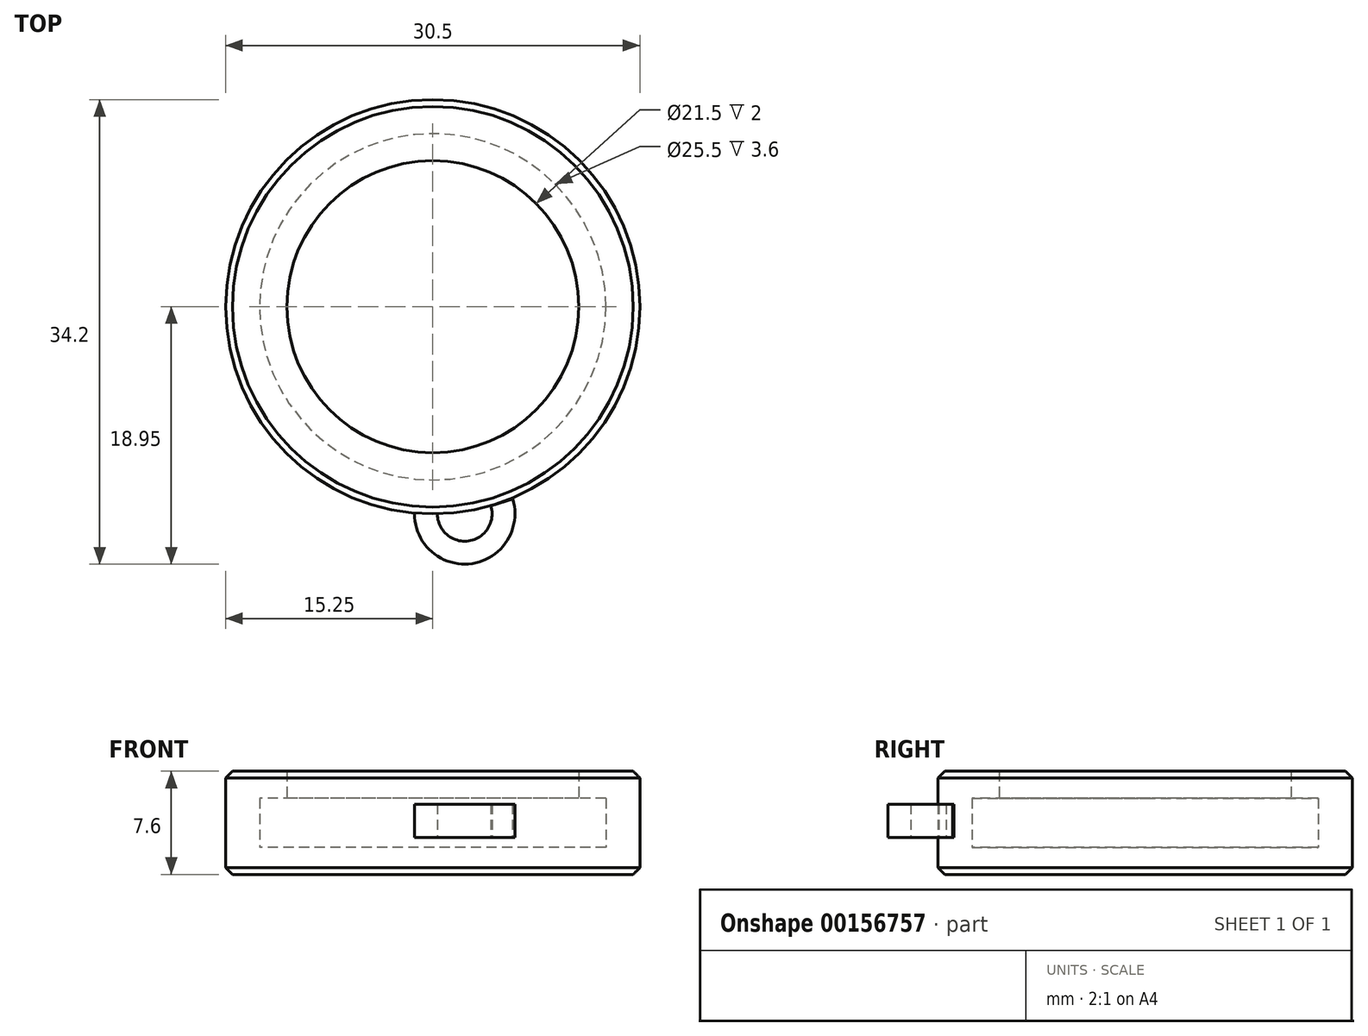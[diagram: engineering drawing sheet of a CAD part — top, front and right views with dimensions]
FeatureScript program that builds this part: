
annotation { "Feature Type Name" : "Feature", "Feature Type Description" : "" }
export const myFeature = defineFeature(function(context is Context, id is Id, definition is map)
    precondition{}
    {
        {
            var Q0;
            Q0=qCreatedBy(makeId("Top.planeOp"),FACE);
            var sketch = newSketch(context, id + "F0", { "sketchPlane" : qUnion([Q0])});
            skCircle(sketch, "E0", {"center": v(0, 0) * mm, "radius": 12.75 * mm});
            skCircle(sketch, "E1.0", {"center": v(0, 0) * mm, "radius": 15.25 * mm});
            skSolve(sketch);
        }
        {
            var Q0;
            Q0=makeQuery(id+"F0.imprint","IMPRINT",FACE,{"disambiguationData":[TD([[makeQuery(id+"F0.imprint","IMPRINT",EDGE,{"derivedFrom":sQuery(id+"F0.wireOp",EDGE,"E0")}),-1.0]])]});
            extrude(context, id + "F1", {"entities" : qUnion([Q0]), "depth" : 3.6 * mm});
        }
        {
            var Q0;
            Q0=makeQuery(id+"F0.imprint","IMPRINT",FACE,{"disambiguationData":[TD([[makeQuery(id+"F0.imprint","IMPRINT",EDGE,{"derivedFrom":sQuery(id+"F0.wireOp",EDGE,"E0")}),1.0]])]});
            var Q1;
            Q1=makeQuery(id+"F0.imprint","IMPRINT",FACE,{"disambiguationData":[TD([[makeQuery(id+"F0.imprint","IMPRINT",EDGE,{"derivedFrom":sQuery(id+"F0.wireOp",EDGE,"E0")}),-1.0]])]});
            extrude(context, id + "F2", {"entities" : qUnion([Q0, Q1]), "operationType" : NewBodyOperationType.ADD, "oppositeDirection" : true, "depth" : 2 * mm});
        }
        {
            var Q0;
            Q0=makeQuery(id+"F2.opExtrude","CAP_EDGE",EDGE,{"disambiguationData":[OSD([sQuery(id+"F0.wireOp",EDGE,"E1.0")])],"isStart":false});
            chamfer(context, id + "F3", {"entities" : qUnion([Q0]), "width" : 0.5 * mm, "tangentPropagation" : true});
        }
        {
            var Q0;
            Q0=makeQuery(id+"F1.opExtrude","CAP_FACE",FACE,{"disambiguationData":[OSD([sQuery(id+"F0.wireOp",EDGE,"E0"),sQuery(id+"F0.wireOp",EDGE,"E1.0")])],"isStart":false});
            var sketch = newSketch(context, id + "F4", { "sketchPlane" : qUnion([Q0])});
            skCircle(sketch, "E2.0", {"center": v(0, 0) * mm, "radius": 10.75 * mm});
            skSolve(sketch);
        }
        {
            var Q0;
            Q0=makeQuery(id+"F4.imprint","IMPRINT",FACE,{"disambiguationData":[TD([[makeQuery(id+"F4.imprint","IMPRINT",EDGE,{"derivedFrom":sQuery(id+"F4.wireOp",EDGE,"E2.0")}),-1.0]])]});
            var Q1;
            Q1=makeQuery(id+"F4.imprint","IMPRINT",FACE,{"disambiguationData":[TD([[makeQuery(id+"F4.imprint","IMPRINT",EDGE,{"derivedFrom":makeQuery(id+"F1.opExtrude","CAP_EDGE",EDGE,{"disambiguationData":[OSD([sQuery(id+"F0.wireOp",EDGE,"E0")])],"isStart":false})}),-1.0]])]});
            extrude(context, id + "F5", {"entities" : qUnion([Q0, Q1]), "operationType" : NewBodyOperationType.ADD, "depth" : 2 * mm});
        }
        {
            var Q0;
            Q0=makeQuery(id+"F5.opExtrude","CAP_EDGE",EDGE,{"disambiguationData":[OSD([sQuery(id+"F0.wireOp",EDGE,"E1.0")])],"isStart":false});
            chamfer(context, id + "F6", {"entities" : qUnion([Q0]), "width" : 0.5 * mm, "tangentPropagation" : true});
        }
        {
            var Q0;
            Q0=qCreatedBy(makeId("Front.planeOp"),FACE);
            cPlane(context, id + "F7", {"entities" : qUnion([Q0]), "cplaneType" : CPlaneType.OFFSET, "offset" : 15.25 * mm, "width" : 150 * mm, "height" : 150 * mm});
        }
        {
            var Q0;
            Q0=qCreatedBy(id+"F7.planeOp",FACE);
            var sketch = newSketch(context, id + "F8", { "sketchPlane" : qUnion([Q0])});
            skLineSegment(sketch, "E3.bottom", {"start": v(-1.35, 3.17) * mm, "end": v(0.33, 3.17) * mm});
            skLineSegment(sketch, "E3.top", {"start": v(-1.35, 0.7) * mm, "end": v(0.33, 0.7) * mm});
            skLineSegment(sketch, "E3.left", {"start": v(-1.35, 3.17) * mm, "end": v(-1.35, 0.7) * mm});
            skLineSegment(sketch, "E3.right", {"start": v(0.33, 3.17) * mm, "end": v(0.33, 0.7) * mm});
            skLineSegment(sketch, "E4", {"start": v(2.35, 3.6) * mm, "end": v(2.35, 0.26) * mm});
            skSolve(sketch);
        }
        {
            var Q0;
            Q0=makeQuery(id+"F8.imprint","IMPRINT",FACE,{"disambiguationData":[TD([[makeQuery(id+"F8.imprint","IMPRINT",EDGE,{"derivedFrom":sQuery(id+"F8.wireOp",EDGE,"E3.bottom")}),-1.0]])]});
            var Q1;
            Q1=sQuery(id+"F8.wireOp",EDGE,"E4");
            revolve(context, id + "F9", {"operationType" : NewBodyOperationType.ADD, "entities" : qUnion([Q0]), "axis" : qUnion([Q1]), "revolveType" : RevolveType.ONE_DIRECTION, "oppositeDirection" : true, "angle" : 197 * degree});
        }
        {
            var Q0;
            Q0=makeQuery(id+"F9.opRevolve","CAP_FACE",FACE,{"disambiguationData":[OSD([sQuery(id+"F8.wireOp",EDGE,"E3.bottom"),sQuery(id+"F8.wireOp",EDGE,"E3.top"),sQuery(id+"F8.wireOp",EDGE,"E3.left"),sQuery(id+"F8.wireOp",EDGE,"E3.right")])],"isStart":false});
            extrude(context, id + "F10", {"entities" : qUnion([Q0]), "endBound" : BoundingType.UP_TO_NEXT, "depth" : 25 * mm});
        }
        {
            var Q0;
            Q0=makeQuery(id+"F9.opRevolve","CAP_FACE",FACE,{"disambiguationData":[OSD([sQuery(id+"F8.wireOp",EDGE,"E3.bottom"),sQuery(id+"F8.wireOp",EDGE,"E3.top"),sQuery(id+"F8.wireOp",EDGE,"E3.left"),sQuery(id+"F8.wireOp",EDGE,"E3.right")])],"isStart":true});
            var Q1;
            {var subQ0=sQuery(id+"F0.wireOp",EDGE,"E1.0");Q1=makeQuery(id+"F5.boolean.opBoolean","MERGE",FACE,{"derivedFrom":[makeQuery(id+"F2.boolean.opBoolean","MERGE",FACE,{"derivedFrom":[makeQuery(id+"F1.opExtrude","SWEPT_FACE",FACE,{"disambiguationData":[OSD([subQ0])]}),makeQuery(id+"F2.opExtrude","SWEPT_FACE",FACE,{"disambiguationData":[OSD([subQ0])]})]}),makeQuery(id+"F5.opExtrude","SWEPT_FACE",FACE,{"disambiguationData":[OSD([subQ0])]})]});}
            extrude(context, id + "F11", {"entities" : qUnion([Q0]), "operationType" : NewBodyOperationType.ADD, "endBound" : BoundingType.UP_TO_NEXT, "endBoundEntityFace" : qUnion([Q1]), "depth" : 25 * mm});
        }
    });
